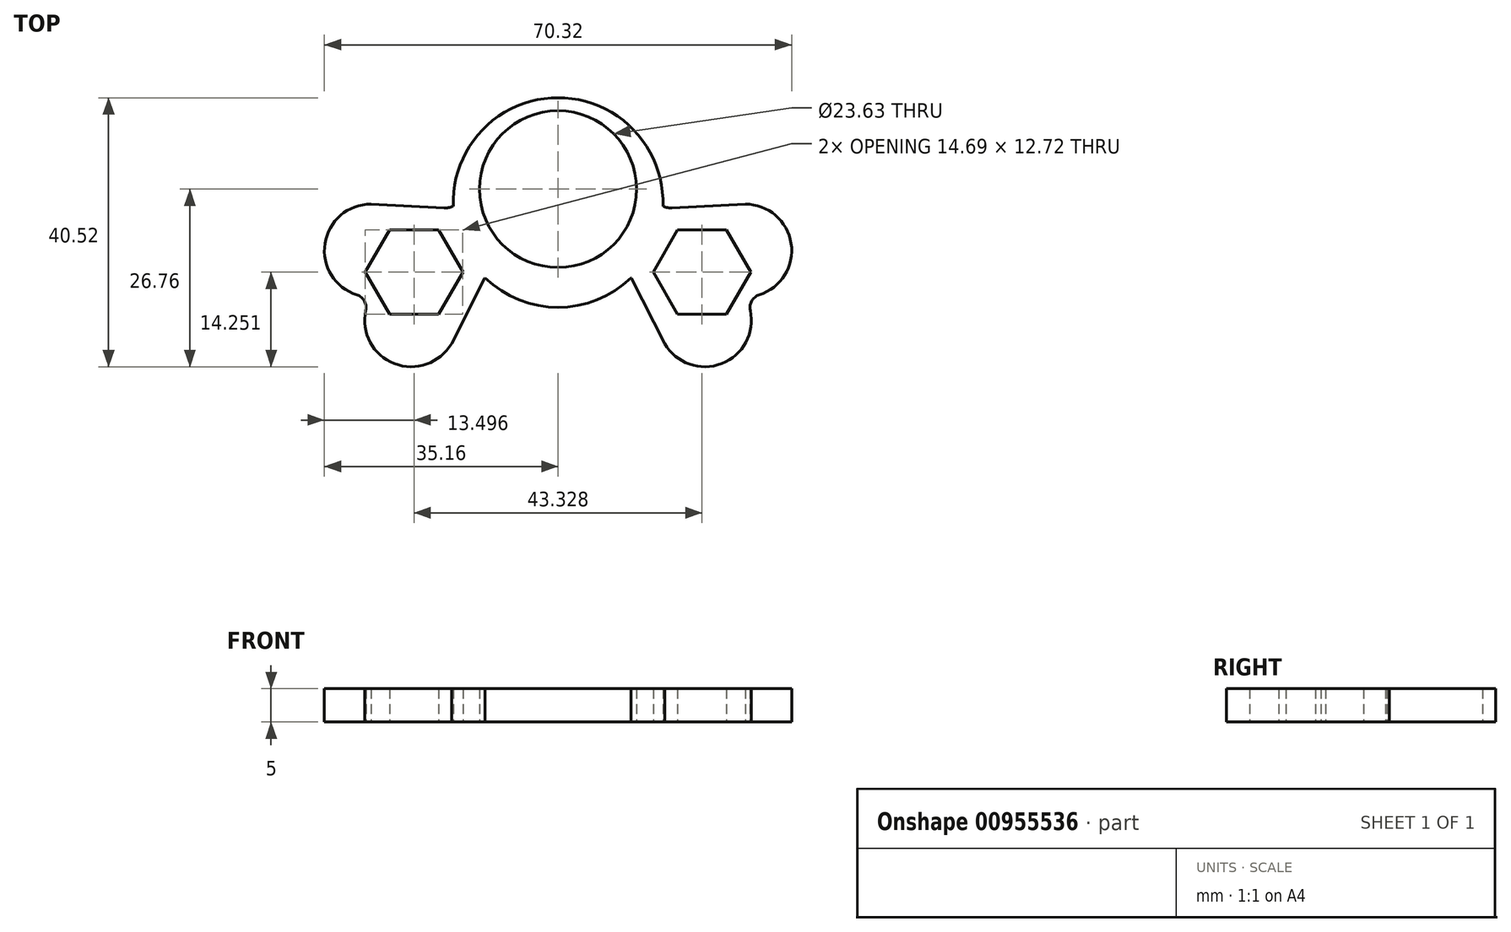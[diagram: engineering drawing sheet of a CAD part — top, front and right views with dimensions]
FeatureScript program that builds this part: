
annotation { "Feature Type Name" : "Feature", "Feature Type Description" : "" }
export const myFeature = defineFeature(function(context is Context, id is Id, definition is map)
    precondition{}
    {
        {
            var Q0;
            Q0=qCreatedBy(makeId("Top.planeOp"),FACE);
            var sketch = newSketch(context, id + "F0", { "sketchPlane" : qUnion([Q0])});
            skLineSegment(sketch, "E0", {"start": v(6.13, 16.29) * mm, "end": v(12.12, 25.52) * mm});
            skArc(sketch, "E1", {"start": v(12.12, 25.52) * mm, "mid": v(10.45, 34.47) * mm, "end": v(1.35, 34.19) * mm});
            skLineSegment(sketch, "E2.trimOffspring", {"start": v(0, 32.52) * mm, "end": v(0, 67.12) * mm, "construction": true});
            skLineSegment(sketch, "E3.trimOffspring", {"start": v(0, 19.02) * mm, "end": v(0, 41.02) * mm, "construction": true});
            skArc(sketch, "E4.MirrorCS", {"start": v(-12.13, 25.52) * mm, "mid": v(-10.45, 34.47) * mm, "end": v(-1.35, 34.19) * mm});
            skPoint(sketch, "E5.visualSharp", {"position": v(0, 32.52) * mm});
            skArc(sketch, "E5.filletArc", {"start": v(-1.35, 34.19) * mm, "mid": v(0, 33.67) * mm, "end": v(1.35, 34.19) * mm});
            skCircle(sketch, "E6.cCircle", {"center": v(0, 25.02) * mm, "radius": 6.36 * mm, "construction": true});
            skLineSegment(sketch, "E6.0", {"start": v(-3.67, 31.38) * mm, "end": v(3.67, 31.38) * mm});
            skLineSegment(sketch, "E6.1", {"start": v(3.67, 31.38) * mm, "end": v(7.34, 25.02) * mm});
            skLineSegment(sketch, "E6.2", {"start": v(7.34, 25.02) * mm, "end": v(3.67, 18.66) * mm});
            skLineSegment(sketch, "E6.3", {"start": v(3.67, 18.66) * mm, "end": v(-3.67, 18.66) * mm});
            skLineSegment(sketch, "E6.4", {"start": v(-3.67, 18.66) * mm, "end": v(-7.35, 25.02) * mm});
            skLineSegment(sketch, "E6.5", {"start": v(-7.35, 25.02) * mm, "end": v(-3.67, 31.38) * mm});
            skPoint(sketch, "E6.0.midPoint", {"position": v(0, 31.38) * mm});
            skCircle(sketch, "E7.0", {"center": v(0, -2.03) * mm, "radius": 15.79 * mm});
            skArc(sketch, "E8", {"start": v(6.13, 16.29) * mm, "mid": v(5.75, 13.89) * mm, "end": v(7.26, 11.99) * mm});
            skPoint(sketch, "E9.orphan", {"position": v(1.19, 8.67) * mm});
            skPoint(sketch, "E10.orphan", {"position": v(-1.19, 8.67) * mm});
            skArc(sketch, "E11.MirrorCS", {"start": v(-6.13, 16.29) * mm, "mid": v(-5.75, 13.89) * mm, "end": v(-7.27, 11.99) * mm});
            skLineSegment(sketch, "E12", {"start": v(-6.13, 16.29) * mm, "end": v(-12.13, 25.52) * mm});
            skLineSegment(sketch, "E13.1.0", {"start": v(-25.34, -6.15) * mm, "end": v(-18, -6.15) * mm});
            skPoint(sketch, "E13.1.1", {"position": v(-28.16, -16.26) * mm});
            skPoint(sketch, "E13.1.2", {"position": v(-27.17, -15.69) * mm});
            skPoint(sketch, "E13.1.3", {"position": v(-8.1, -3.3) * mm});
            skArc(sketch, "E13.1.4", {"start": v(-28.16, -2.26) * mm, "mid": v(-35.08, -8.18) * mm, "end": v(-30.28, -15.93) * mm});
            skCircle(sketch, "E13.1.5", {"center": v(-21.66, -12.5) * mm, "radius": 6.36 * mm, "construction": true});
            skArc(sketch, "E13.1.6", {"start": v(-17.17, -2.83) * mm, "mid": v(-14.9, -1.97) * mm, "end": v(-14.02, 0.3) * mm});
            skLineSegment(sketch, "E13.1.7", {"start": v(-11.04, -13.45) * mm, "end": v(-16.03, -23.26) * mm});
            skLineSegment(sketch, "E13.1.8", {"start": v(-16.47, -9.5) * mm, "end": v(-35.52, -20.5) * mm, "construction": true});
            skLineSegment(sketch, "E13.1.9", {"start": v(-14.32, -12.5) * mm, "end": v(-18, -18.87) * mm});
            skLineSegment(sketch, "E13.1.10", {"start": v(-29, -12.5) * mm, "end": v(-25.34, -6.15) * mm});
            skArc(sketch, "E13.1.11", {"start": v(-16.03, -23.26) * mm, "mid": v(-24.62, -26.29) * mm, "end": v(-28.93, -18.26) * mm});
            skLineSegment(sketch, "E13.1.12", {"start": v(-17.17, -2.83) * mm, "end": v(-28.16, -2.26) * mm});
            skLineSegment(sketch, "E13.1.13", {"start": v(-18, -18.87) * mm, "end": v(-25.34, -18.87) * mm});
            skPoint(sketch, "E13.1.14", {"position": v(-6.92, -5.37) * mm});
            skLineSegment(sketch, "E13.1.15", {"start": v(-18, -6.15) * mm, "end": v(-14.32, -12.5) * mm});
            skArc(sketch, "E13.1.16", {"start": v(-11.04, -13.45) * mm, "mid": v(-9.15, -11.92) * mm, "end": v(-6.75, -12.29) * mm});
            skArc(sketch, "E13.1.17", {"start": v(-28.93, -18.26) * mm, "mid": v(-29.16, -16.83) * mm, "end": v(-30.28, -15.93) * mm});
            skLineSegment(sketch, "E13.1.18", {"start": v(-25.34, -18.87) * mm, "end": v(-29, -12.5) * mm});
            skLineSegment(sketch, "E13.2.0", {"start": v(18, -18.87) * mm, "end": v(14.32, -12.5) * mm});
            skPoint(sketch, "E13.2.1", {"position": v(28.16, -16.26) * mm});
            skPoint(sketch, "E13.2.2", {"position": v(27.17, -15.69) * mm});
            skPoint(sketch, "E13.2.3", {"position": v(6.92, -5.36) * mm});
            skArc(sketch, "E13.2.4", {"start": v(16.04, -23.26) * mm, "mid": v(24.63, -26.28) * mm, "end": v(28.94, -18.26) * mm});
            skCircle(sketch, "E13.2.5", {"center": v(21.66, -12.5) * mm, "radius": 6.36 * mm, "construction": true});
            skArc(sketch, "E13.2.6", {"start": v(11.04, -13.45) * mm, "mid": v(9.15, -11.92) * mm, "end": v(6.75, -12.29) * mm});
            skLineSegment(sketch, "E13.2.7", {"start": v(17.17, -2.83) * mm, "end": v(28.16, -2.26) * mm});
            skLineSegment(sketch, "E13.2.8", {"start": v(16.47, -9.5) * mm, "end": v(35.52, -20.5) * mm, "construction": true});
            skLineSegment(sketch, "E13.2.9", {"start": v(18, -6.15) * mm, "end": v(25.34, -6.15) * mm});
            skLineSegment(sketch, "E13.2.10", {"start": v(25.34, -18.87) * mm, "end": v(18, -18.87) * mm});
            skArc(sketch, "E13.2.11", {"start": v(28.16, -2.26) * mm, "mid": v(35.08, -8.18) * mm, "end": v(30.28, -15.93) * mm});
            skLineSegment(sketch, "E13.2.12", {"start": v(11.04, -13.45) * mm, "end": v(16.04, -23.26) * mm});
            skLineSegment(sketch, "E13.2.13", {"start": v(25.34, -6.15) * mm, "end": v(29, -12.5) * mm});
            skPoint(sketch, "E13.2.14", {"position": v(8.1, -3.3) * mm});
            skLineSegment(sketch, "E13.2.15", {"start": v(14.32, -12.5) * mm, "end": v(18, -6.15) * mm});
            skArc(sketch, "E13.2.16", {"start": v(17.17, -2.83) * mm, "mid": v(14.9, -1.97) * mm, "end": v(14.02, 0.3) * mm});
            skArc(sketch, "E13.2.17", {"start": v(30.28, -15.93) * mm, "mid": v(29.16, -16.83) * mm, "end": v(28.94, -18.26) * mm});
            skLineSegment(sketch, "E13.2.18", {"start": v(29, -12.5) * mm, "end": v(25.34, -18.87) * mm});
            skPoint(sketch, "E13.center", {"position": v(0, 0) * mm});
            skCircle(sketch, "E14", {"center": v(0, 0) * mm, "radius": 11.81 * mm});
            skSolve(sketch);
        }
        {
            var Q0;
            Q0=makeQuery(id+"F0.imprint","IMPRINT",FACE,{"disambiguationData":[TD([[makeQuery(id+"F0.imprint","IMPRINT",EDGE,{"derivedFrom":sQuery(id+"F0.wireOp",EDGE,"E13.1.0")}),1.0]])]});
            var Q1;
            {var subQ0=sQuery(id+"F0.wireOp",EDGE,"E7.0");var subQ4=makeQuery(id+"F0.imprint","INTERSECT",VERTEX,{"derivedFrom":[subQ0,sQuery(id+"F0.wireOp",EDGE,"E8")]});Q1=makeQuery(id+"F0.imprint","IMPRINT",FACE,{"disambiguationData":[TD([[makeQuery(id+"F0.imprint","IMPRINT",EDGE,{"disambiguationData":[TD([[subQ4,1.0]])],"derivedFrom":subQ0}),1.0]])]});}
            var Q2;
            Q2=makeQuery(id+"F0.imprint","IMPRINT",FACE,{"disambiguationData":[TD([[makeQuery(id+"F0.imprint","IMPRINT",EDGE,{"derivedFrom":sQuery(id+"F0.wireOp",EDGE,"E13.2.0")}),1.0]])]});
            var Q3;
            Q3=makeQuery(id+"F0.imprint","IMPRINT",FACE,{"disambiguationData":[TD([[makeQuery(id+"F0.imprint","IMPRINT",EDGE,{"derivedFrom":sQuery(id+"F0.wireOp",EDGE,"E0")}),1.0]])]});
            extrude(context, id + "F1", {"entities" : qUnion([Q0, Q1, Q2, Q3]), "depth" : 5 * mm, "offsetDistance" : 25 * mm});
        }
    });
